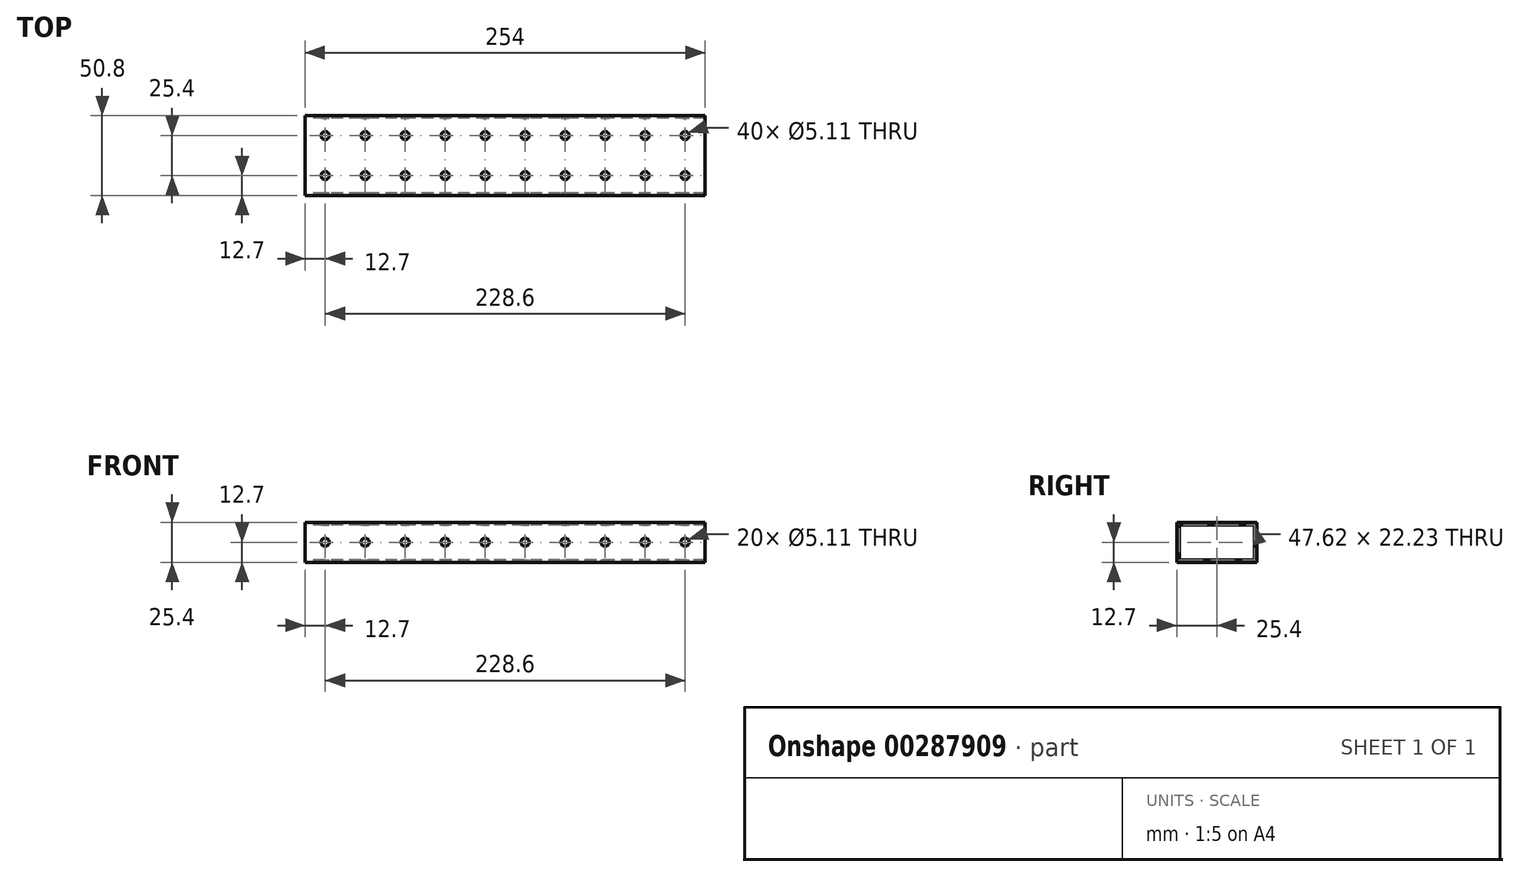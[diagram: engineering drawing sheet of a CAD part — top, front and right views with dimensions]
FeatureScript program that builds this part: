
annotation { "Feature Type Name" : "Feature", "Feature Type Description" : "" }
export const myFeature = defineFeature(function(context is Context, id is Id, definition is map)
    precondition{}
    {
        {
            var Q0;
            Q0=qCreatedBy(makeId("Right.planeOp"),FACE);
            var sketch = newSketch(context, id + "F0", { "sketchPlane" : qUnion([Q0])});
            skLineSegment(sketch, "E0.bottom", {"start": v(25.4, 12.7) * mm, "end": v(-25.4, 12.7) * mm});
            skLineSegment(sketch, "E0.top", {"start": v(25.4, -12.7) * mm, "end": v(-25.4, -12.7) * mm});
            skLineSegment(sketch, "E0.left", {"start": v(25.4, 12.7) * mm, "end": v(25.4, -12.7) * mm});
            skLineSegment(sketch, "E0.right", {"start": v(-25.4, 12.7) * mm, "end": v(-25.4, -12.7) * mm});
            skPoint(sketch, "E0.middle", {"position": v(0, 0) * mm});
            skLineSegment(sketch, "E1.bottom", {"start": v(23.81, 11.11) * mm, "end": v(-23.81, 11.11) * mm});
            skLineSegment(sketch, "E1.top", {"start": v(23.81, -11.11) * mm, "end": v(-23.81, -11.11) * mm});
            skLineSegment(sketch, "E1.left", {"start": v(23.81, 11.11) * mm, "end": v(23.81, -11.11) * mm});
            skLineSegment(sketch, "E1.right", {"start": v(-23.81, 11.11) * mm, "end": v(-23.81, -11.11) * mm});
            skSolve(sketch);
        }
        {
            var Q0;
            Q0=qSketchRegion(id+"F0",true);
            extrude(context, id + "F1", {"entities" : qUnion([Q0]), "depth" : 254 * mm});
        }
        {
            var Q0;
            Q0=makeQuery(id+"F1.opExtrude","SWEPT_FACE",FACE,{"disambiguationData":[OSD([sQuery(id+"F0.wireOp",EDGE,"E0.bottom")])]});
            var sketch = newSketch(context, id + "F2", { "sketchPlane" : qUnion([Q0])});
            skCircle(sketch, "E2", {"center": v(12.7, 12.7) * mm, "radius": 2.55 * mm});
            skCircle(sketch, "E3.0.1.0", {"center": v(12.7, -12.7) * mm, "radius": 2.55 * mm});
            skCircle(sketch, "E3.1.0.0", {"center": v(38.1, 12.7) * mm, "radius": 2.55 * mm});
            skCircle(sketch, "E3.1.1.0", {"center": v(38.1, -12.7) * mm, "radius": 2.55 * mm});
            skCircle(sketch, "E3.2.0.0", {"center": v(63.5, 12.7) * mm, "radius": 2.55 * mm});
            skCircle(sketch, "E3.2.1.0", {"center": v(63.5, -12.7) * mm, "radius": 2.55 * mm});
            skCircle(sketch, "E3.3.0.0", {"center": v(88.9, 12.7) * mm, "radius": 2.55 * mm});
            skCircle(sketch, "E3.3.1.0", {"center": v(88.9, -12.7) * mm, "radius": 2.55 * mm});
            skCircle(sketch, "E3.4.0.0", {"center": v(114.3, 12.7) * mm, "radius": 2.55 * mm});
            skCircle(sketch, "E3.4.1.0", {"center": v(114.3, -12.7) * mm, "radius": 2.55 * mm});
            skCircle(sketch, "E3.5.0.0", {"center": v(139.7, 12.7) * mm, "radius": 2.55 * mm});
            skCircle(sketch, "E3.5.1.0", {"center": v(139.7, -12.7) * mm, "radius": 2.55 * mm});
            skCircle(sketch, "E3.6.0.0", {"center": v(165.1, 12.7) * mm, "radius": 2.55 * mm});
            skCircle(sketch, "E3.6.1.0", {"center": v(165.1, -12.7) * mm, "radius": 2.55 * mm});
            skCircle(sketch, "E3.7.0.0", {"center": v(190.5, 12.7) * mm, "radius": 2.55 * mm});
            skCircle(sketch, "E3.7.1.0", {"center": v(190.5, -12.7) * mm, "radius": 2.55 * mm});
            skCircle(sketch, "E3.8.0.0", {"center": v(215.9, 12.7) * mm, "radius": 2.55 * mm});
            skCircle(sketch, "E3.8.1.0", {"center": v(215.9, -12.7) * mm, "radius": 2.55 * mm});
            skCircle(sketch, "E3.9.0.0", {"center": v(241.3, 12.7) * mm, "radius": 2.55 * mm});
            skCircle(sketch, "E3.9.1.0", {"center": v(241.3, -12.7) * mm, "radius": 2.55 * mm});
            skLineSegment(sketch, "E3.direction1", {"start": v(12.7, 12.7) * mm, "end": v(38.1, 12.7) * mm, "construction": true});
            skLineSegment(sketch, "E3.direction2", {"start": v(12.7, 12.7) * mm, "end": v(12.7, -12.7) * mm, "construction": true});
            skSolve(sketch);
        }
        {
            var Q0;
            Q0=sQuery(id+"F2.wireOp",VERTEX,"E3.1.1.0.center");
            var Q1;
            Q1=sQuery(id+"F2.wireOp",VERTEX,"E3.2.0.0.center");
            var Q2;
            Q2=sQuery(id+"F2.wireOp",VERTEX,"E3.2.1.0.center");
            var Q3;
            Q3=sQuery(id+"F2.wireOp",VERTEX,"E3.3.0.0.center");
            var Q4;
            Q4=sQuery(id+"F2.wireOp",VERTEX,"E3.3.1.0.center");
            var Q5;
            Q5=sQuery(id+"F2.wireOp",VERTEX,"E3.4.0.0.center");
            var Q6;
            Q6=sQuery(id+"F2.wireOp",VERTEX,"E3.9.1.0.center");
            var Q7;
            Q7=sQuery(id+"F2.wireOp",VERTEX,"E3.8.1.0.center");
            var Q8;
            Q8=sQuery(id+"F2.wireOp",VERTEX,"E3.7.1.0.center");
            var Q9;
            Q9=sQuery(id+"F2.wireOp",VERTEX,"E3.6.1.0.center");
            var Q10;
            Q10=sQuery(id+"F2.wireOp",VERTEX,"E3.9.0.0.center");
            var Q11;
            Q11=sQuery(id+"F2.wireOp",VERTEX,"E3.8.0.0.center");
            var Q12;
            Q12=sQuery(id+"F2.wireOp",VERTEX,"E3.4.1.0.center");
            var Q13;
            Q13=sQuery(id+"F2.wireOp",VERTEX,"E3.7.0.0.center");
            var Q14;
            Q14=sQuery(id+"F2.wireOp",VERTEX,"E3.5.0.0.center");
            var Q15;
            Q15=sQuery(id+"F2.wireOp",VERTEX,"E3.5.1.0.center");
            var Q16;
            Q16=sQuery(id+"F2.wireOp",VERTEX,"E3.6.0.0.center");
            var Q17;
            Q17=sQuery(id+"F2.wireOp",VERTEX,"E2.center");
            var Q18;
            Q18=sQuery(id+"F2.wireOp",VERTEX,"E3.0.1.0.center");
            var Q19;
            Q19=sQuery(id+"F2.wireOp",VERTEX,"E3.1.0.0.center");
            var Q20;
            Q20=makeQuery(id+"F1.opExtrude","SWEPT_BODY",BODY,{"disambiguationData":[OSD([sQuery(id+"F0.wireOp",EDGE,"E0.bottom"),sQuery(id+"F0.wireOp",EDGE,"E0.top"),sQuery(id+"F0.wireOp",EDGE,"E0.left"),sQuery(id+"F0.wireOp",EDGE,"E0.right"),sQuery(id+"F0.wireOp",EDGE,"E1.bottom"),sQuery(id+"F0.wireOp",EDGE,"E1.top"),sQuery(id+"F0.wireOp",EDGE,"E1.left"),sQuery(id+"F0.wireOp",EDGE,"E1.right")])]});
            hole(context, id + "F3", {"style" : HoleStyle.SIMPLE, "endStyle" : HoleEndStyle.THROUGH, "holeDiameter" : 5.1 * mm, "tappedDepth" : 12.7 * mm, "tapClearance" : 3, "locations" : qUnion([Q0, Q1, Q2, Q3, Q4, Q5, Q6, Q7, Q8, Q9, Q10, Q11, Q12, Q13, Q14, Q15, Q16, Q17, Q18, Q19]), "scope" : qUnion([Q20])});
        }
        {
            var Q0;
            Q0=makeQuery(id+"F1.opExtrude","SWEPT_FACE",FACE,{"disambiguationData":[OSD([sQuery(id+"F0.wireOp",EDGE,"E0.left")])]});
            var sketch = newSketch(context, id + "F4", { "sketchPlane" : qUnion([Q0])});
            skCircle(sketch, "E4", {"center": v(-241.3, 0) * mm, "radius": 2.55 * mm});
            skCircle(sketch, "E5.1.0.0", {"center": v(-215.9, 0) * mm, "radius": 2.55 * mm});
            skCircle(sketch, "E5.2.0.0", {"center": v(-190.5, 0) * mm, "radius": 2.55 * mm});
            skCircle(sketch, "E5.3.0.0", {"center": v(-165.1, 0) * mm, "radius": 2.55 * mm});
            skCircle(sketch, "E5.4.0.0", {"center": v(-139.7, 0) * mm, "radius": 2.55 * mm});
            skCircle(sketch, "E5.5.0.0", {"center": v(-114.3, 0) * mm, "radius": 2.55 * mm});
            skCircle(sketch, "E5.6.0.0", {"center": v(-88.9, 0) * mm, "radius": 2.55 * mm});
            skCircle(sketch, "E5.7.0.0", {"center": v(-63.5, 0) * mm, "radius": 2.55 * mm});
            skCircle(sketch, "E5.8.0.0", {"center": v(-38.1, 0) * mm, "radius": 2.55 * mm});
            skCircle(sketch, "E5.9.0.0", {"center": v(-12.7, 0) * mm, "radius": 2.55 * mm});
            skLineSegment(sketch, "E5.direction1", {"start": v(-241.3, 0) * mm, "end": v(-215.9, 0) * mm, "construction": true});
            skSolve(sketch);
        }
        {
            var Q0;
            Q0=sQuery(id+"F4.wireOp",VERTEX,"E5.1.0.0.center");
            var Q1;
            Q1=sQuery(id+"F4.wireOp",VERTEX,"E5.3.0.0.center");
            var Q2;
            Q2=sQuery(id+"F4.wireOp",VERTEX,"E5.2.0.0.center");
            var Q3;
            Q3=sQuery(id+"F4.wireOp",VERTEX,"E5.4.0.0.center");
            var Q4;
            Q4=sQuery(id+"F4.wireOp",VERTEX,"E5.direction1.start");
            var Q5;
            Q5=sQuery(id+"F4.wireOp",VERTEX,"E5.5.0.0.center");
            var Q6;
            Q6=sQuery(id+"F4.wireOp",VERTEX,"E5.7.0.0.center");
            var Q7;
            Q7=sQuery(id+"F4.wireOp",VERTEX,"E5.6.0.0.center");
            var Q8;
            Q8=sQuery(id+"F4.wireOp",VERTEX,"E5.9.0.0.center");
            var Q9;
            Q9=sQuery(id+"F4.wireOp",VERTEX,"E5.8.0.0.center");
            var Q10;
            Q10=makeQuery(id+"F1.opExtrude","SWEPT_BODY",BODY,{"disambiguationData":[OSD([sQuery(id+"F0.wireOp",EDGE,"E0.bottom"),sQuery(id+"F0.wireOp",EDGE,"E0.top"),sQuery(id+"F0.wireOp",EDGE,"E0.left"),sQuery(id+"F0.wireOp",EDGE,"E0.right"),sQuery(id+"F0.wireOp",EDGE,"E1.bottom"),sQuery(id+"F0.wireOp",EDGE,"E1.top"),sQuery(id+"F0.wireOp",EDGE,"E1.left"),sQuery(id+"F0.wireOp",EDGE,"E1.right")])]});
            hole(context, id + "F5", {"style" : HoleStyle.SIMPLE, "endStyle" : HoleEndStyle.THROUGH, "holeDiameter" : 5.1 * mm, "tappedDepth" : 12.7 * mm, "tapClearance" : 3, "locations" : qUnion([Q0, Q1, Q2, Q3, Q4, Q5, Q6, Q7, Q8, Q9]), "scope" : qUnion([Q10])});
        }
    });
